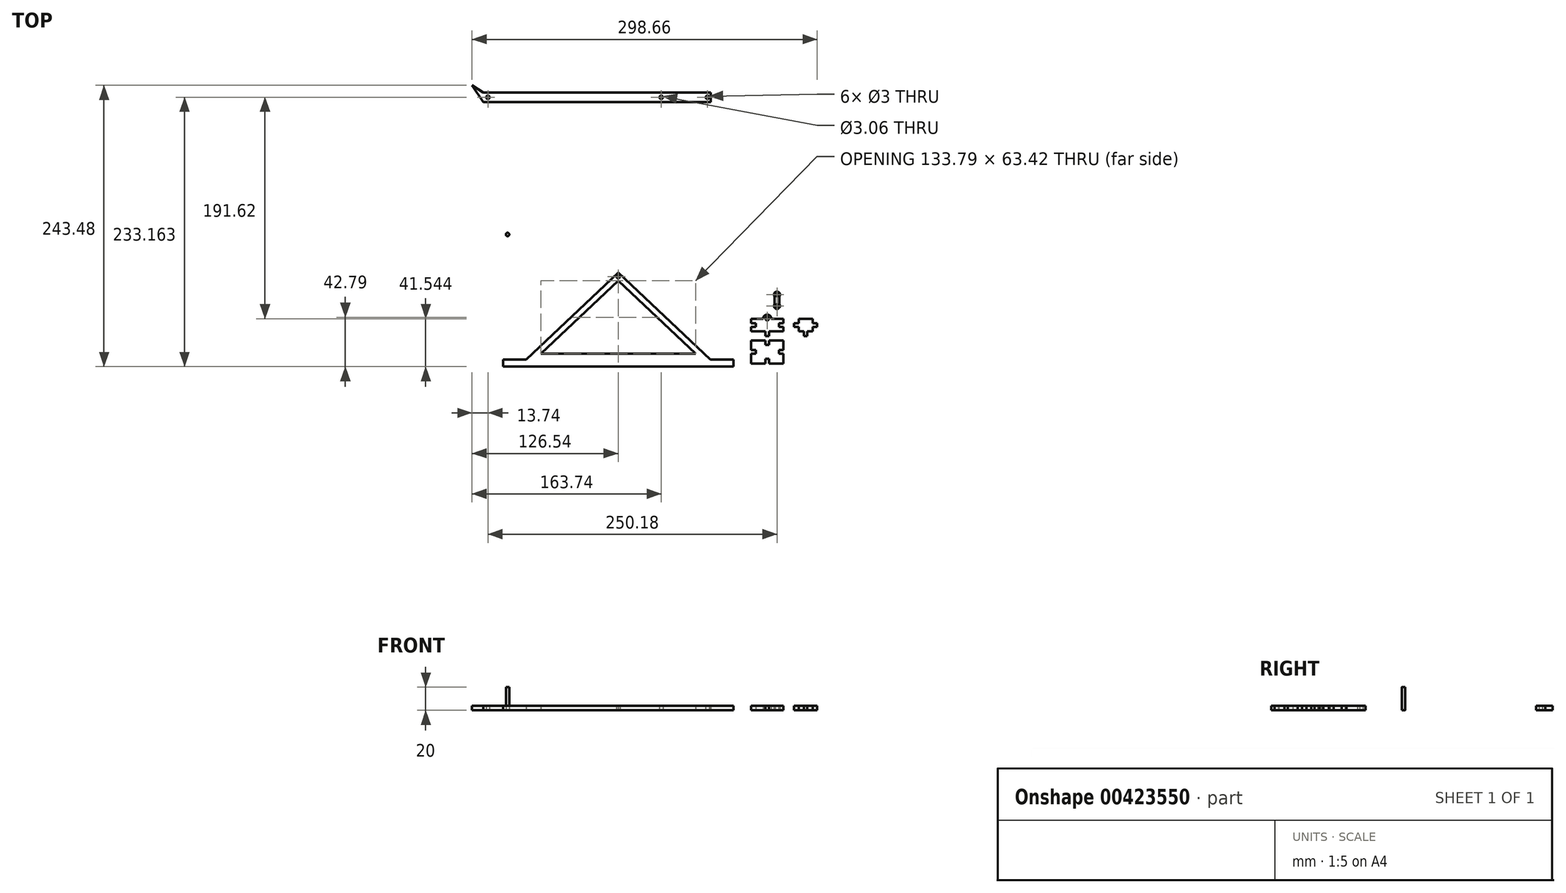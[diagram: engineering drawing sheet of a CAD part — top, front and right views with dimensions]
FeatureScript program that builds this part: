
annotation { "Feature Type Name" : "Feature", "Feature Type Description" : "" }
export const myFeature = defineFeature(function(context is Context, id is Id, definition is map)
    precondition{}
    {
        {
            var Q0;
            Q0=qCreatedBy(makeId("Top.planeOp"),FACE);
            var sketch = newSketch(context, id + "F0", { "sketchPlane" : qUnion([Q0])});
            skLineSegment(sketch, "E0", {"start": v(-116.84, 3) * mm, "end": v(42.44, 3) * mm});
            skLineSegment(sketch, "E1", {"start": v(42.44, 3) * mm, "end": v(-37.2, 78.5) * mm});
            skLineSegment(sketch, "E2", {"start": v(-37.2, 78.5) * mm, "end": v(-116.84, 3) * mm});
            skLineSegment(sketch, "E3", {"start": v(-116.84, 3) * mm, "end": v(-136.84, 3) * mm});
            skLineSegment(sketch, "E4", {"start": v(-136.84, 3) * mm, "end": v(-136.84, -3) * mm});
            skLineSegment(sketch, "E5", {"start": v(-136.84, -3) * mm, "end": v(62.44, -3) * mm});
            skLineSegment(sketch, "E6", {"start": v(62.44, -3) * mm, "end": v(62.44, 3) * mm});
            skLineSegment(sketch, "E7", {"start": v(62.44, 3) * mm, "end": v(42.44, 3) * mm});
            skLineSegment(sketch, "E8.0", {"start": v(-37.2, 71.5) * mm, "end": v(-104.1, 8.08) * mm});
            skLineSegment(sketch, "E8.1", {"start": v(29.7, 8.08) * mm, "end": v(-37.2, 71.5) * mm});
            skLineSegment(sketch, "E8.2", {"start": v(-104.1, 8.08) * mm, "end": v(29.7, 8.08) * mm});
            skCircle(sketch, "E9", {"center": v(-37.2, 75) * mm, "radius": 1.5 * mm});
            skLineSegment(sketch, "E10.left", {"start": v(98.02, 57.94) * mm, "end": v(98.02, 51) * mm});
            skLineSegment(sketch, "E10.right", {"start": v(102.34, 57.94) * mm, "end": v(102.34, 51) * mm});
            skArc(sketch, "E11", {"start": v(98.02, 51) * mm, "mid": v(100.18, 46.97) * mm, "end": v(102.34, 51) * mm});
            skLineSegment(sketch, "E12.bottom", {"start": v(77.76, 38.54) * mm, "end": v(105.76, 38.54) * mm});
            skLineSegment(sketch, "E12.top", {"start": v(77.76, 27.54) * mm, "end": v(90.26, 27.54) * mm});
            skLineSegment(sketch, "E12.left", {"start": v(77.76, 38.54) * mm, "end": v(77.76, 34.54) * mm});
            skLineSegment(sketch, "E12.right", {"start": v(105.76, 38.54) * mm, "end": v(105.76, 34.54) * mm});
            skArc(sketch, "E13", {"start": v(95.26, 38.54) * mm, "mid": v(91.76, 42.04) * mm, "end": v(88.26, 38.54) * mm});
            skLineSegment(sketch, "E14.bottom", {"start": v(118.97, 38.54) * mm, "end": v(130.97, 38.54) * mm});
            skLineSegment(sketch, "E14.top", {"start": v(118.97, 27.54) * mm, "end": v(123.47, 27.54) * mm});
            skLineSegment(sketch, "E14.left", {"start": v(118.97, 38.54) * mm, "end": v(118.97, 34.54) * mm});
            skLineSegment(sketch, "E14.right", {"start": v(130.97, 38.54) * mm, "end": v(130.97, 34.54) * mm});
            skLineSegment(sketch, "E15.bottom", {"start": v(77.76, 19.78) * mm, "end": v(90.26, 19.78) * mm});
            skLineSegment(sketch, "E15.top", {"start": v(77.76, -0.22) * mm, "end": v(90.26, -0.22) * mm});
            skLineSegment(sketch, "E15.left", {"start": v(77.76, 19.78) * mm, "end": v(77.76, 9.78) * mm});
            skLineSegment(sketch, "E15.right", {"start": v(105.76, 19.78) * mm, "end": v(105.76, 11.28) * mm});
            skLineSegment(sketch, "E16.bottom", {"start": v(-154, 234.16) * mm, "end": v(43, 234.16) * mm});
            skLineSegment(sketch, "E16.top", {"start": v(-154, 226.16) * mm, "end": v(43, 226.16) * mm});
            skLineSegment(sketch, "E16.left", {"start": v(-154, 234.16) * mm, "end": v(-154, 226.16) * mm});
            skLineSegment(sketch, "E16.right", {"start": v(43, 234.16) * mm, "end": v(43, 226.16) * mm});
            skCircle(sketch, "E17", {"center": v(0, 230.16) * mm, "radius": 1.53 * mm});
            skCircle(sketch, "E18", {"center": v(40, 230.16) * mm, "radius": 1.5 * mm});
            skCircle(sketch, "E19", {"center": v(-150, 230.16) * mm, "radius": 1.5 * mm});
            skLineSegment(sketch, "E20", {"start": v(98.02, 54.47) * mm, "end": v(107.6, 54.47) * mm, "construction": true});
            skPoint(sketch, "E20.endSnap0", {"position": v(102.34, 54.47) * mm});
            skArc(sketch, "E21.MirrorCS", {"start": v(98.02, 57.94) * mm, "mid": v(100.18, 61.97) * mm, "end": v(102.34, 57.94) * mm});
            skLineSegment(sketch, "E22.MirrorCS", {"start": v(98.02, 51) * mm, "end": v(98.02, 57.94) * mm});
            skLineSegment(sketch, "E23.MirrorCS", {"start": v(102.34, 51) * mm, "end": v(102.34, 57.94) * mm});
            skCircle(sketch, "E24", {"center": v(100.18, 59.38) * mm, "radius": 1.5 * mm});
            skCircle(sketch, "E25", {"center": v(100.18, 49.57) * mm, "radius": 1.5 * mm});
            skCircle(sketch, "E26", {"center": v(91.76, 38.54) * mm, "radius": 1.5 * mm});
            skLineSegment(sketch, "E27.bottom", {"start": v(115.02, 34.54) * mm, "end": v(118.97, 34.54) * mm});
            skLineSegment(sketch, "E27.top", {"start": v(115.02, 31.54) * mm, "end": v(118.97, 31.54) * mm});
            skLineSegment(sketch, "E27.left", {"start": v(115.02, 34.54) * mm, "end": v(115.02, 31.54) * mm});
            skPoint(sketch, "E27.middle", {"position": v(118.97, 33.04) * mm});
            skLineSegment(sketch, "E28", {"start": v(124.97, 38.54) * mm, "end": v(124.97, 27.54) * mm, "construction": true});
            skLineSegment(sketch, "E29.MirrorCS", {"start": v(134.92, 34.54) * mm, "end": v(134.92, 31.54) * mm});
            skPoint(sketch, "E30.MirrorP", {"position": v(130.97, 33.04) * mm});
            skLineSegment(sketch, "E31.MirrorCS", {"start": v(134.92, 31.54) * mm, "end": v(130.97, 31.54) * mm});
            skLineSegment(sketch, "E32.MirrorCS", {"start": v(134.92, 34.54) * mm, "end": v(130.97, 34.54) * mm});
            skLineSegment(sketch, "E33.bottom", {"start": v(126.47, 23.54) * mm, "end": v(123.47, 23.54) * mm});
            skLineSegment(sketch, "E33.left", {"start": v(126.47, 23.54) * mm, "end": v(126.47, 27.54) * mm});
            skLineSegment(sketch, "E33.right", {"start": v(123.47, 23.54) * mm, "end": v(123.47, 27.54) * mm});
            skPoint(sketch, "E33.middle", {"position": v(124.97, 27.54) * mm});
            skPoint(sketch, "E27.right.start.orphan", {"position": v(122.92, 34.54) * mm});
            skPoint(sketch, "E34.orphan", {"position": v(122.92, 31.54) * mm});
            skPoint(sketch, "E35.orphan", {"position": v(123.47, 31.54) * mm});
            skPoint(sketch, "E36.orphan", {"position": v(126.47, 31.54) * mm});
            skPoint(sketch, "E37.orphan", {"position": v(127.02, 31.54) * mm});
            skPoint(sketch, "E38.orphan", {"position": v(127.02, 34.54) * mm});
            skLineSegment(sketch, "E39.trimOffspring", {"start": v(130.97, 31.54) * mm, "end": v(130.97, 27.54) * mm});
            skLineSegment(sketch, "E40.trimOffspring", {"start": v(118.97, 31.54) * mm, "end": v(118.97, 27.54) * mm});
            skLineSegment(sketch, "E41.trimOffspring", {"start": v(126.47, 27.54) * mm, "end": v(130.97, 27.54) * mm});
            skLineSegment(sketch, "E42.bottom", {"start": v(93.26, 23.54) * mm, "end": v(90.26, 23.54) * mm});
            skLineSegment(sketch, "E42.left", {"start": v(93.26, 23.54) * mm, "end": v(93.26, 27.54) * mm});
            skLineSegment(sketch, "E42.right", {"start": v(90.26, 23.54) * mm, "end": v(90.26, 27.54) * mm});
            skPoint(sketch, "E42.middle", {"position": v(91.76, 27.54) * mm});
            skPoint(sketch, "E43.orphan", {"position": v(90.26, 31.54) * mm});
            skPoint(sketch, "E44.orphan", {"position": v(93.26, 31.54) * mm});
            skLineSegment(sketch, "E45.trimOffspring", {"start": v(93.26, 27.54) * mm, "end": v(105.76, 27.54) * mm});
            skLineSegment(sketch, "E46.bottom", {"start": v(93.26, 15.78) * mm, "end": v(90.26, 15.78) * mm});
            skLineSegment(sketch, "E46.left", {"start": v(93.26, 15.78) * mm, "end": v(93.26, 19.78) * mm});
            skLineSegment(sketch, "E46.right", {"start": v(90.26, 15.78) * mm, "end": v(90.26, 19.78) * mm});
            skPoint(sketch, "E46.middle", {"position": v(91.76, 19.78) * mm});
            skPoint(sketch, "E46.top.end.orphan", {"position": v(90.26, 23.78) * mm});
            skPoint(sketch, "E47.orphan", {"position": v(93.26, 23.78) * mm});
            skLineSegment(sketch, "E48.trimOffspring", {"start": v(93.26, 19.78) * mm, "end": v(105.76, 19.78) * mm});
            skLineSegment(sketch, "E49", {"start": v(77.76, 9.78) * mm, "end": v(105.76, 9.78) * mm, "construction": true});
            skLineSegment(sketch, "E50.MirrorCS", {"start": v(93.26, 3.78) * mm, "end": v(90.26, 3.78) * mm});
            skPoint(sketch, "E51.MirrorP", {"position": v(91.76, -0.22) * mm});
            skLineSegment(sketch, "E52.MirrorCS", {"start": v(90.26, 3.78) * mm, "end": v(90.26, -0.22) * mm});
            skLineSegment(sketch, "E53.MirrorCS", {"start": v(93.26, 3.78) * mm, "end": v(93.26, -0.22) * mm});
            skLineSegment(sketch, "E54.trimOffspring", {"start": v(93.26, -0.22) * mm, "end": v(105.76, -0.22) * mm});
            skLineSegment(sketch, "E55.bottom", {"start": v(81.76, 11.28) * mm, "end": v(77.76, 11.28) * mm});
            skLineSegment(sketch, "E55.top", {"start": v(81.76, 8.28) * mm, "end": v(77.76, 8.28) * mm});
            skLineSegment(sketch, "E55.left", {"start": v(81.76, 11.28) * mm, "end": v(81.76, 8.28) * mm});
            skPoint(sketch, "E55.middle", {"position": v(40.56, 12.78) * mm});
            skLineSegment(sketch, "E56", {"start": v(91.76, 15.78) * mm, "end": v(91.76, 3.78) * mm, "construction": true});
            skPoint(sketch, "E57.MirrorP", {"position": v(105.76, 9.78) * mm});
            skLineSegment(sketch, "E58.MirrorCS", {"start": v(101.76, 11.28) * mm, "end": v(101.76, 8.28) * mm});
            skLineSegment(sketch, "E59.MirrorCS", {"start": v(101.76, 8.28) * mm, "end": v(105.76, 8.28) * mm});
            skLineSegment(sketch, "E60.MirrorCS", {"start": v(101.76, 11.28) * mm, "end": v(105.76, 11.28) * mm});
            skPoint(sketch, "E61.orphan", {"position": v(109.76, 11.28) * mm});
            skPoint(sketch, "E62.orphan", {"position": v(109.76, 8.28) * mm});
            skLineSegment(sketch, "E63.trimOffspring", {"start": v(105.76, 8.28) * mm, "end": v(105.76, -0.22) * mm});
            skPoint(sketch, "E55.right.start.orphan", {"position": v(73.76, 11.28) * mm});
            skPoint(sketch, "E64.orphan", {"position": v(73.76, 8.28) * mm});
            skLineSegment(sketch, "E65.trimOffspring", {"start": v(77.76, 8.28) * mm, "end": v(77.76, -0.22) * mm});
            skLineSegment(sketch, "E66.bottom", {"start": v(81.76, 34.54) * mm, "end": v(77.76, 34.54) * mm});
            skLineSegment(sketch, "E66.top", {"start": v(81.76, 31.54) * mm, "end": v(77.76, 31.54) * mm});
            skLineSegment(sketch, "E66.left", {"start": v(81.76, 34.54) * mm, "end": v(81.76, 31.54) * mm});
            skPoint(sketch, "E66.middle", {"position": v(40.56, 36.04) * mm});
            skPoint(sketch, "E66.right.start.orphan", {"position": v(73.76, 34.54) * mm});
            skPoint(sketch, "E67.orphan", {"position": v(73.76, 31.54) * mm});
            skLineSegment(sketch, "E68.trimOffspring", {"start": v(77.76, 31.54) * mm, "end": v(77.76, 27.54) * mm});
            skLineSegment(sketch, "E69.bottom", {"start": v(101.76, 34.54) * mm, "end": v(105.76, 34.54) * mm});
            skLineSegment(sketch, "E69.top", {"start": v(101.76, 31.54) * mm, "end": v(105.76, 31.54) * mm});
            skLineSegment(sketch, "E69.left", {"start": v(101.76, 34.54) * mm, "end": v(101.76, 31.54) * mm});
            skPoint(sketch, "E69.middle", {"position": v(105.76, 33.04) * mm});
            skPoint(sketch, "E69.right.end.orphan", {"position": v(109.76, 31.54) * mm});
            skPoint(sketch, "E70.orphan", {"position": v(109.76, 34.54) * mm});
            skLineSegment(sketch, "E71.trimOffspring", {"start": v(105.76, 31.54) * mm, "end": v(105.76, 27.54) * mm});
            skPoint(sketch, "E72", {"position": v(43, 230.16) * mm});
            skLineSegment(sketch, "E73", {"start": v(-154, 226.16) * mm, "end": v(-163.74, 240.48) * mm});
            skLineSegment(sketch, "E74", {"start": v(-163.74, 240.48) * mm, "end": v(-154, 234.16) * mm});
            skCircle(sketch, "E75", {"center": v(-132.95, 111.42) * mm, "radius": 1.45 * mm});
            skSolve(sketch);
        }
        {
            var Q0;
            Q0=makeQuery(id+"F0.imprint","IMPRINT",FACE,{"disambiguationData":[TD([[makeQuery(id+"F0.imprint","IMPRINT",EDGE,{"derivedFrom":sQuery(id+"F0.wireOp",EDGE,"E0")}),-1.0]])]});
            var Q1;
            {var subQ0=sQuery(id+"F0.wireOp",EDGE,"E15.bottom");Q1=makeQuery(id+"F0.imprint","IMPRINT",FACE,{"disambiguationData":[TD([[makeQuery(id+"F0.imprint","IMPRINT",EDGE,{"derivedFrom":subQ0}),-1.0]])]});}
            var Q2;
            Q2=makeQuery(id+"F0.imprint","IMPRINT",FACE,{"disambiguationData":[TD([[makeQuery(id+"F0.imprint","IMPRINT",EDGE,{"derivedFrom":sQuery(id+"F0.wireOp",EDGE,"E0")}),1.0]])]});
            var Q3;
            Q3=makeQuery(id+"F0.imprint","IMPRINT",FACE,{"disambiguationData":[TD([[makeQuery(id+"F0.imprint","IMPRINT",EDGE,{"derivedFrom":sQuery(id+"F0.wireOp",EDGE,"E16.left")}),-1.0]])]});
            var Q4;
            Q4=makeQuery(id+"F0.imprint","IMPRINT",FACE,{"disambiguationData":[TD([[makeQuery(id+"F0.imprint","IMPRINT",EDGE,{"derivedFrom":sQuery(id+"F0.wireOp",EDGE,"E16.bottom")}),-1.0]])]});
            var Q5;
            Q5=makeQuery(id+"F0.imprint","IMPRINT",FACE,{"disambiguationData":[TD([[makeQuery(id+"F0.imprint","IMPRINT",EDGE,{"derivedFrom":sQuery(id+"F0.wireOp",EDGE,"E14.bottom")}),-1.0]])]});
            var Q6;
            Q6=makeQuery(id+"F0.imprint","IMPRINT",FACE,{"disambiguationData":[TD([[makeQuery(id+"F0.imprint","IMPRINT",EDGE,{"derivedFrom":sQuery(id+"F0.wireOp",EDGE,"E12.top")}),1.0]])]});
            var Q7;
            {var subQ0=sQuery(id+"F0.wireOp",EDGE,"E13");Q7=makeQuery(id+"F0.imprint","IMPRINT",FACE,{"disambiguationData":[TD([[makeQuery(id+"F0.imprint","IMPRINT",EDGE,{"derivedFrom":subQ0}),1.0]])]});}
            var Q8;
            Q8=makeQuery(id+"F0.imprint","IMPRINT",FACE,{"disambiguationData":[TD([[makeQuery(id+"F0.imprint","IMPRINT",EDGE,{"derivedFrom":sQuery(id+"F0.wireOp",EDGE,"E11")}),1.0]])]});
            extrude(context, id + "F1", {"entities" : qUnion([Q0, Q1, Q2, Q3, Q4, Q5, Q6, Q7, Q8]), "depth" : 4 * mm});
        }
        {
            var Q0;
            Q0=makeQuery(id+"F0.imprint","IMPRINT",FACE,{"disambiguationData":[TD([[makeQuery(id+"F0.imprint","IMPRINT",EDGE,{"derivedFrom":sQuery(id+"F0.wireOp",EDGE,"E75")}),1.0]])]});
            extrude(context, id + "F2", {"entities" : qUnion([Q0]), "depth" : 20 * mm});
        }
    });
